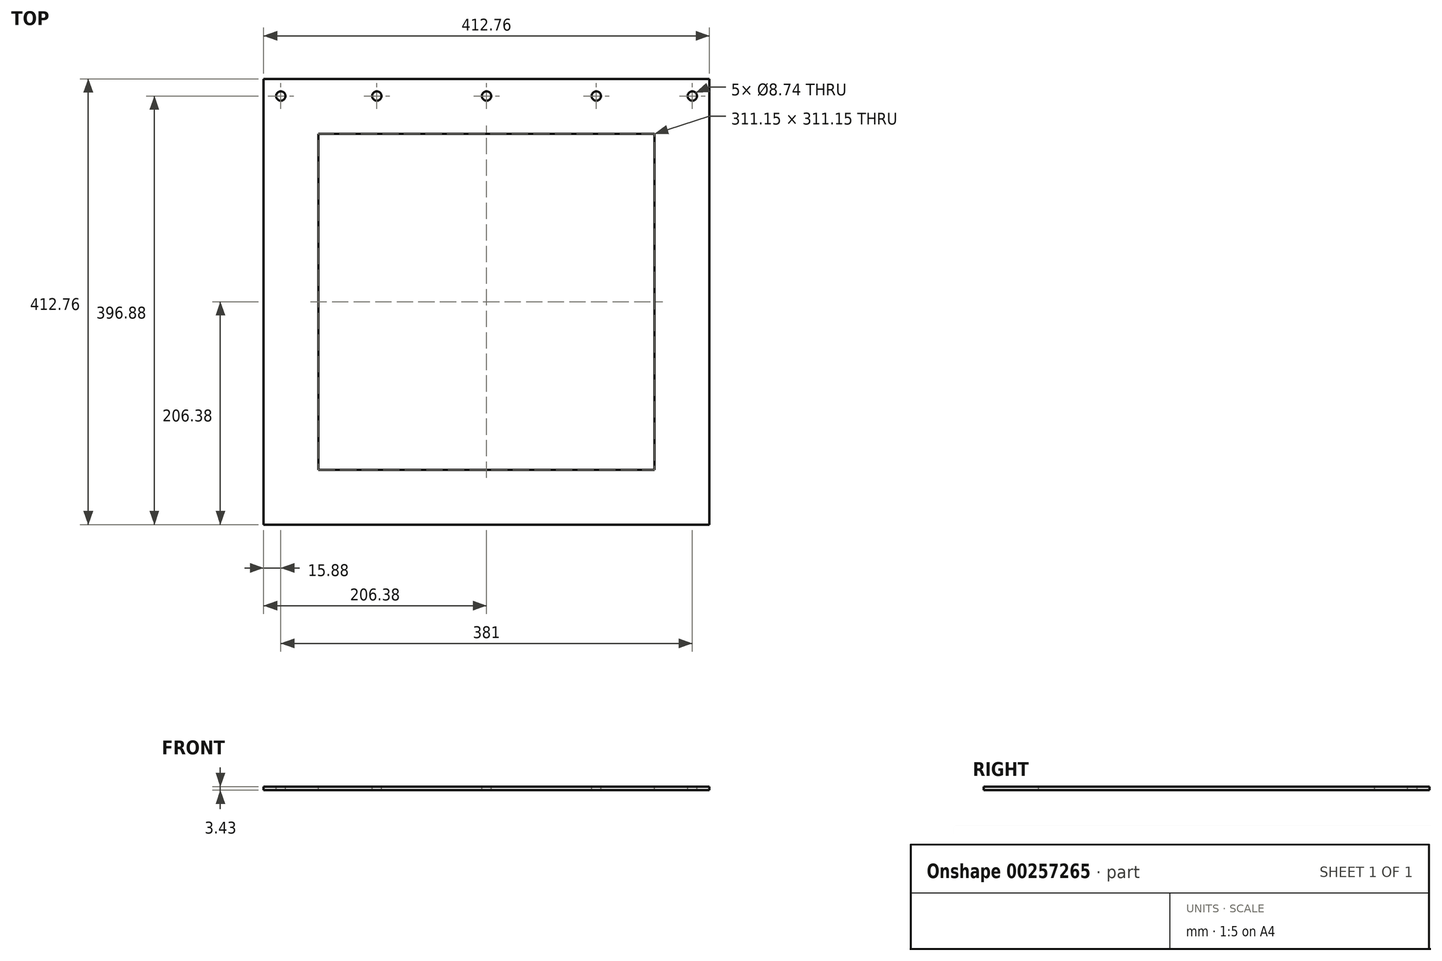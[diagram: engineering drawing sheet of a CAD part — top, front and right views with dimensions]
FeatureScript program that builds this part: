
annotation { "Feature Type Name" : "Feature", "Feature Type Description" : "" }
export const myFeature = defineFeature(function(context is Context, id is Id, definition is map)
    precondition{}
    {
        {
            var Q0;
            Q0=qCreatedBy(makeId("Top.planeOp"),FACE);
            var sketch = newSketch(context, id + "F0", { "sketchPlane" : qUnion([Q0])});
            skLineSegment(sketch, "E0.bottom", {"start": v(-206.38, -206.37) * mm, "end": v(206.38, -206.37) * mm});
            skLineSegment(sketch, "E0.top", {"start": v(-206.38, 206.38) * mm, "end": v(206.38, 206.38) * mm});
            skLineSegment(sketch, "E0.left", {"start": v(-206.38, -206.37) * mm, "end": v(-206.38, 206.38) * mm});
            skLineSegment(sketch, "E0.right", {"start": v(206.38, -206.37) * mm, "end": v(206.38, 206.38) * mm});
            skPoint(sketch, "E0.middle", {"position": v(0, 0) * mm});
            skLineSegment(sketch, "E1.bottom", {"start": v(-155.58, -155.58) * mm, "end": v(155.58, -155.58) * mm});
            skLineSegment(sketch, "E1.top", {"start": v(-155.58, 155.58) * mm, "end": v(155.58, 155.58) * mm});
            skLineSegment(sketch, "E1.left", {"start": v(-155.57, -155.58) * mm, "end": v(-155.58, 155.58) * mm});
            skLineSegment(sketch, "E1.right", {"start": v(155.58, -155.58) * mm, "end": v(155.57, 155.58) * mm});
            skPoint(sketch, "E2", {"position": v(-190.5, 190.5) * mm});
            skPoint(sketch, "E3", {"position": v(-101.6, 190.5) * mm});
            skPoint(sketch, "E4", {"position": v(0, 190.5) * mm});
            skPoint(sketch, "E5", {"position": v(101.6, 190.5) * mm});
            skPoint(sketch, "E6", {"position": v(190.5, 190.5) * mm});
            skSolve(sketch);
        }
        {
            var Q0;
            Q0=makeQuery(id+"F0.imprint","IMPRINT",FACE,{"disambiguationData":[TD([[makeQuery(id+"F0.imprint","IMPRINT",EDGE,{"derivedFrom":sQuery(id+"F0.wireOp",EDGE,"E0.bottom")}),1.0]])]});
            extrude(context, id + "F1", {"entities" : qUnion([Q0]), "oppositeDirection" : true, "depth" : 3.43 * mm});
        }
        {
            var Q0;
            Q0=sQuery(id+"F0.wireOp",VERTEX,"E2");
            var Q1;
            Q1=sQuery(id+"F0.wireOp",VERTEX,"E3");
            var Q2;
            Q2=sQuery(id+"F0.wireOp",VERTEX,"E4");
            var Q3;
            Q3=sQuery(id+"F0.wireOp",VERTEX,"E5");
            var Q4;
            Q4=sQuery(id+"F0.wireOp",VERTEX,"E6");
            var Q5;
            Q5=makeQuery(id+"F1.opExtrude","SWEPT_BODY",BODY,{"disambiguationData":[OSD([sQuery(id+"F0.wireOp",EDGE,"E0.bottom"),sQuery(id+"F0.wireOp",EDGE,"E0.top"),sQuery(id+"F0.wireOp",EDGE,"E0.left"),sQuery(id+"F0.wireOp",EDGE,"E0.right"),sQuery(id+"F0.wireOp",EDGE,"E1.bottom"),sQuery(id+"F0.wireOp",EDGE,"E1.top"),sQuery(id+"F0.wireOp",EDGE,"E1.left"),sQuery(id+"F0.wireOp",EDGE,"E1.right")])]});
            hole(context, id + "F2", {"style" : HoleStyle.SIMPLE, "endStyle" : HoleEndStyle.THROUGH, "holeDiameter" : 8.74 * mm, "tappedDepth" : 12.7 * mm, "tapClearance" : 3, "locations" : qUnion([Q0, Q1, Q2, Q3, Q4]), "scope" : qUnion([Q5])});
        }
        {
            var Q0;
            Q0=qCreatedBy(makeId("Front.planeOp"),FACE);
            var sketch = newSketch(context, id + "F3", { "sketchPlane" : qUnion([Q0])});
            skLineSegment(sketch, "E7", {"start": v(0, 0) * mm, "end": v(0, 74.96) * mm});
            skSolve(sketch);
        }
    });
